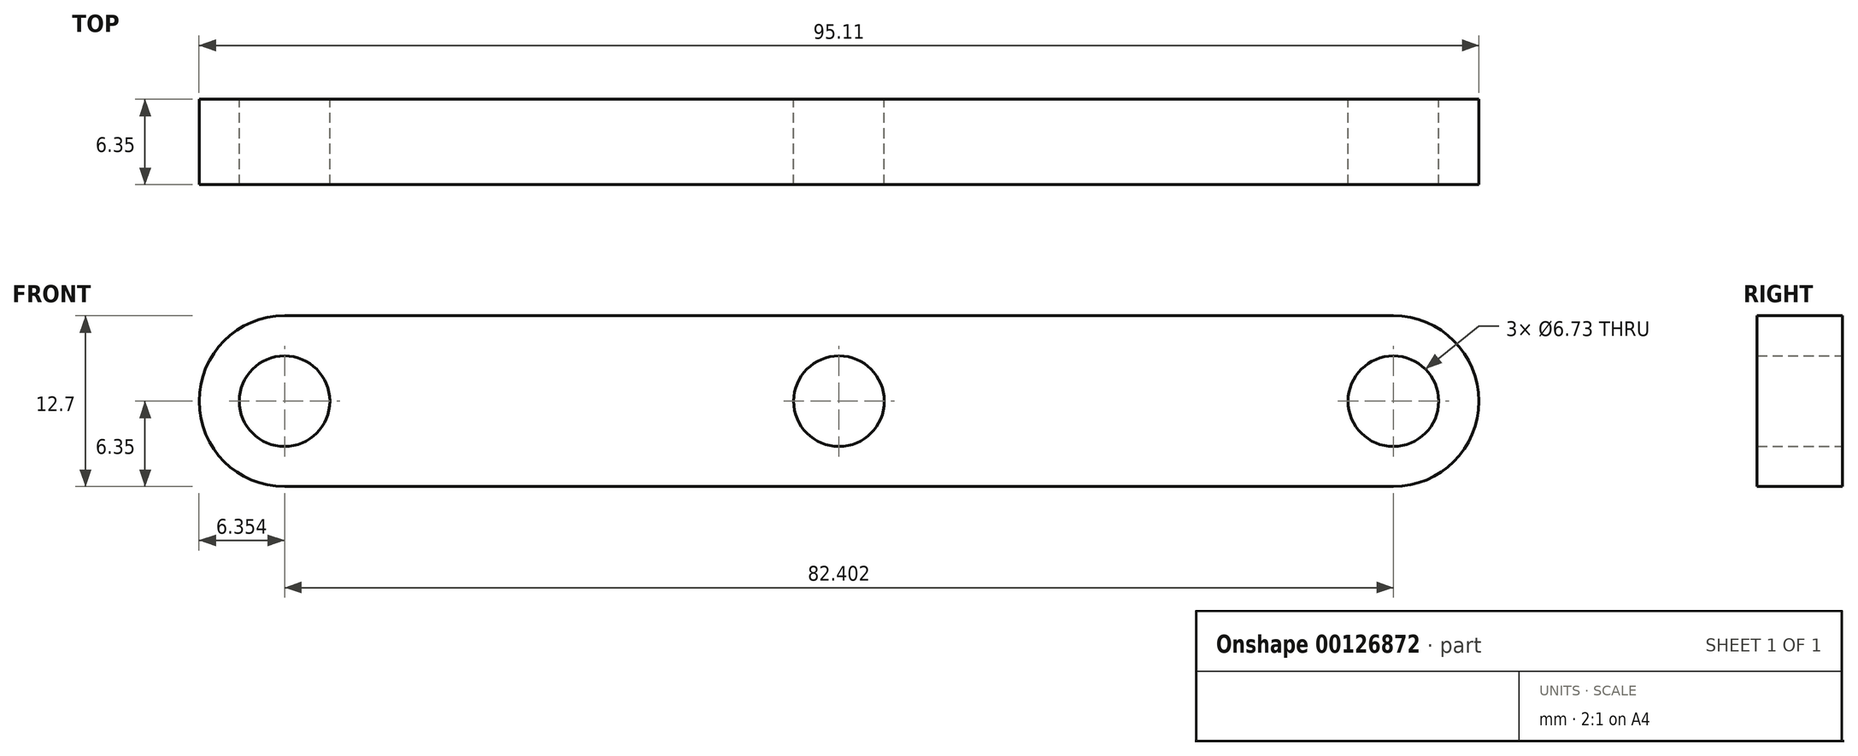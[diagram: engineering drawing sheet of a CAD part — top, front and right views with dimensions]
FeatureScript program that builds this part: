
annotation { "Feature Type Name" : "Feature", "Feature Type Description" : "" }
export const myFeature = defineFeature(function(context is Context, id is Id, definition is map)
    precondition{}
    {
        {
            var Q0;
            Q0=qCreatedBy(makeId("Front.planeOp"),FACE);
            var sketch = newSketch(context, id + "F0", { "sketchPlane" : qUnion([Q0])});
            skLineSegment(sketch, "E0.bottom", {"start": v(52.28, 0) * mm, "end": v(-30.13, 0) * mm});
            skLineSegment(sketch, "E0.top", {"start": v(52.28, 12.7) * mm, "end": v(-30.13, 12.7) * mm});
            skLineSegment(sketch, "E0.left", {"start": v(52.28, 0) * mm, "end": v(52.28, 12.7) * mm});
            skLineSegment(sketch, "E0.right", {"start": v(-30.13, 0) * mm, "end": v(-30.13, 12.7) * mm});
            skArc(sketch, "E1", {"start": v(-30.13, 12.7) * mm, "mid": v(-36.48, 6.35) * mm, "end": v(-30.13, 0) * mm});
            skArc(sketch, "E2", {"start": v(52.28, 0) * mm, "mid": v(58.63, 6.35) * mm, "end": v(52.28, 12.7) * mm});
            skCircle(sketch, "E3", {"center": v(52.28, 6.35) * mm, "radius": 3.37 * mm});
            skCircle(sketch, "E4", {"center": v(-30.13, 6.35) * mm, "radius": 3.37 * mm});
            skCircle(sketch, "E5", {"center": v(11.08, 6.35) * mm, "radius": 3.37 * mm});
            skPoint(sketch, "E5.centerSnap0", {"position": v(11.08, 0) * mm});
            skSolve(sketch);
        }
        {
            var Q0;
            {var subQ0=sQuery(id+"F0.wireOp",EDGE,"E2");Q0=makeQuery(id+"F0.imprint","IMPRINT",FACE,{"disambiguationData":[TD([[makeQuery(id+"F0.imprint","IMPRINT",EDGE,{"derivedFrom":subQ0}),1.0]])]});}
            var Q1;
            {var subQ0=sQuery(id+"F0.wireOp",EDGE,"E1");Q1=makeQuery(id+"F0.imprint","IMPRINT",FACE,{"disambiguationData":[TD([[makeQuery(id+"F0.imprint","IMPRINT",EDGE,{"derivedFrom":subQ0}),1.0]])]});}
            var Q2;
            {var subQ5=sQuery(id+"F0.wireOp",EDGE,"E0.bottom");Q2=makeQuery(id+"F0.imprint","IMPRINT",FACE,{"disambiguationData":[TD([[makeQuery(id+"F0.imprint","IMPRINT",EDGE,{"derivedFrom":subQ5}),-1.0]])]});}
            extrude(context, id + "F1", {"entities" : qUnion([Q0, Q1, Q2]), "depth" : 6.35 * mm});
        }
    });
